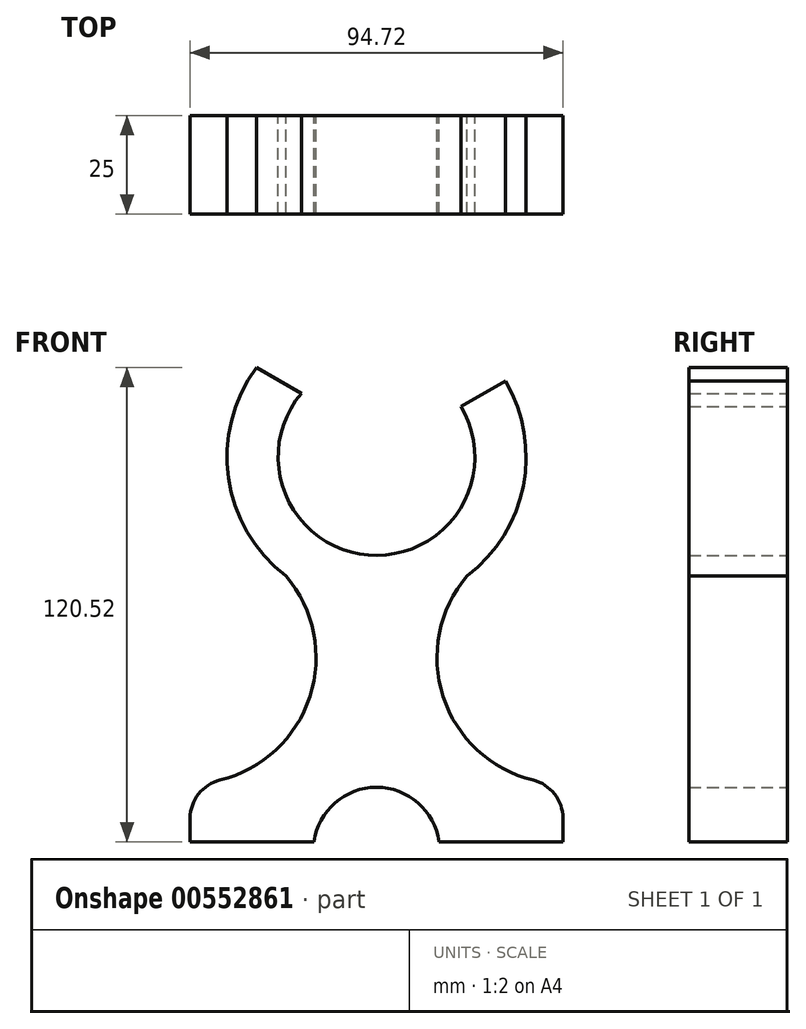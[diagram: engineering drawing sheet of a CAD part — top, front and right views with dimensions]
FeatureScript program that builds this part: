
annotation { "Feature Type Name" : "Feature", "Feature Type Description" : "" }
export const myFeature = defineFeature(function(context is Context, id is Id, definition is map)
    precondition{}
    {
        {
            var Q0;
            Q0=qCreatedBy(makeId("Front.planeOp"),FACE);
            var sketch = newSketch(context, id + "F0", { "sketchPlane" : qUnion([Q0])});
            skArc(sketch, "E0", {"start": v(-30.45, 72.13) * mm, "mid": v(-37.63, 44.1) * mm, "end": v(-23, 19.14) * mm});
            skArc(sketch, "E1", {"start": v(-19.07, 65.56) * mm, "mid": v(-2.07, 24.48) * mm, "end": v(21.48, 62.19) * mm});
            skLineSegment(sketch, "E2", {"start": v(21.48, 62.19) * mm, "end": v(32.74, 68.69) * mm});
            skLineSegment(sketch, "E3", {"start": v(-19.07, 65.56) * mm, "end": v(-30.45, 72.13) * mm});
            skArc(sketch, "E4", {"start": v(-39.74, -32.68) * mm, "mid": v(-16.9, -11.44) * mm, "end": v(-23, 19.14) * mm});
            skArc(sketch, "E5.MirrorC", {"start": v(39.74, -32.68) * mm, "mid": v(16.9, -11.44) * mm, "end": v(23, 19.14) * mm});
            skLineSegment(sketch, "E6", {"start": v(-47.36, -42.4) * mm, "end": v(-47.36, -48.4) * mm});
            skLineSegment(sketch, "E7.MirrorCS", {"start": v(47.36, -42.4) * mm, "end": v(47.36, -48.4) * mm});
            skPoint(sketch, "E8.visualSharp", {"position": v(-47.36, -33.6) * mm});
            skArc(sketch, "E8.filletArc", {"start": v(-39.74, -32.68) * mm, "mid": v(-45.23, -36.22) * mm, "end": v(-47.36, -42.4) * mm});
            skPoint(sketch, "E9.visualSharp", {"position": v(47.36, -33.6) * mm});
            skArc(sketch, "E9.filletArc", {"start": v(47.36, -42.4) * mm, "mid": v(45.23, -36.22) * mm, "end": v(39.74, -32.68) * mm});
            skLineSegment(sketch, "E10", {"start": v(-47.36, -48.4) * mm, "end": v(-15.86, -48.4) * mm});
            skArc(sketch, "E11", {"start": v(15.86, -48.4) * mm, "mid": v(0, -34.52) * mm, "end": v(-15.86, -48.4) * mm});
            skLineSegment(sketch, "E12.trimOffspring", {"start": v(15.86, -48.4) * mm, "end": v(47.36, -48.4) * mm});
            skArc(sketch, "E13.trimOffspring", {"start": v(23, 19.14) * mm, "mid": v(37.29, 42.06) * mm, "end": v(32.74, 68.69) * mm});
            skSolve(sketch);
        }
        {
            var Q0;
            Q0 = qSketchRegion(id + "F0", true);
            extrude(context, id + "F1", {"entities" : qUnion([Q0]), "depth" : 25 * mm, "offsetDistance" : 25 * mm});
        }
        {
            var Q0;
            Q0 = qSketchRegion(id + "F0", true);
            extrude(context, id + "F2", {"entities" : qUnion([Q0]), "depth" : 25 * mm, "offsetDistance" : 25 * mm});
        }
    });
